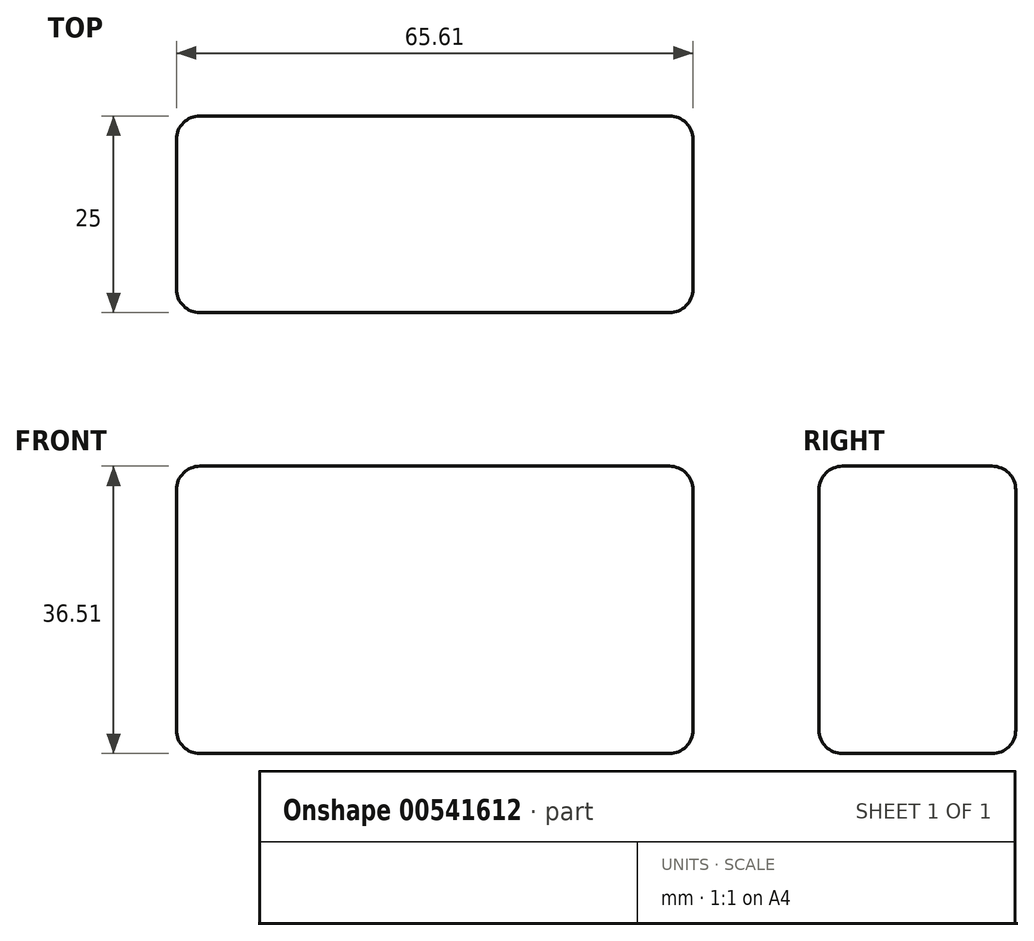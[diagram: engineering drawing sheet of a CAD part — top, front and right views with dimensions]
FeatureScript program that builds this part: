
annotation { "Feature Type Name" : "Feature", "Feature Type Description" : "" }
export const myFeature = defineFeature(function(context is Context, id is Id, definition is map)
    precondition{}
    {
        {
            var Q0;
            Q0=qCreatedBy(makeId("Front.planeOp"),FACE);
            var sketch = newSketch(context, id + "F0", { "sketchPlane" : qUnion([Q0])});
            skLineSegment(sketch, "E0.bottom", {"start": v(-30.55, 25.56) * mm, "end": v(35.06, 25.56) * mm});
            skLineSegment(sketch, "E0.top", {"start": v(-30.55, -10.95) * mm, "end": v(35.06, -10.95) * mm});
            skLineSegment(sketch, "E0.left", {"start": v(-30.55, 25.56) * mm, "end": v(-30.55, -10.95) * mm});
            skLineSegment(sketch, "E0.right", {"start": v(35.06, 25.56) * mm, "end": v(35.06, -10.95) * mm});
            skSolve(sketch);
        }
        {
            var Q0;
            Q0=makeQuery(id+"F0.imprint","IMPRINT",FACE,{"disambiguationData":[TD([[makeQuery(id+"F0.imprint","IMPRINT",EDGE,{"derivedFrom":sQuery(id+"F0.wireOp",EDGE,"E0.bottom")}),-1.0]])]});
            extrude(context, id + "F1", {"entities" : qUnion([Q0]), "depth" : 25 * mm, "offsetDistance" : 25 * mm});
        }
        {
            var Q0;
            Q0=makeQuery(id+"F1.opExtrude","CAP_EDGE",EDGE,{"disambiguationData":[OSD([sQuery(id+"F0.wireOp",EDGE,"E0.bottom")])],"isStart":false});
            var Q1;
            Q1=makeQuery(id+"F1.opExtrude","CAP_EDGE",EDGE,{"disambiguationData":[OSD([sQuery(id+"F0.wireOp",EDGE,"E0.bottom")])],"isStart":true});
            var Q2;
            Q2=makeQuery(id+"F1.opExtrude","CAP_EDGE",EDGE,{"disambiguationData":[OSD([sQuery(id+"F0.wireOp",EDGE,"E0.top")])],"isStart":false});
            var Q3;
            Q3=makeQuery(id+"F1.opExtrude","CAP_EDGE",EDGE,{"disambiguationData":[OSD([sQuery(id+"F0.wireOp",EDGE,"E0.right")])],"isStart":false});
            var Q4;
            Q4=makeQuery(id+"F1.opExtrude","SWEPT_EDGE",EDGE,{"disambiguationData":[OSD([sQuery(id+"F0.wireOp",EDGE,"E0.bottom"),sQuery(id+"F0.wireOp",EDGE,"E0.right")])]});
            var Q5;
            Q5=makeQuery(id+"F1.opExtrude","SWEPT_FACE",FACE,{"disambiguationData":[OSD([sQuery(id+"F0.wireOp",EDGE,"E0.top")])]});
            var Q6;
            Q6=makeQuery(id+"F1.opExtrude","CAP_EDGE",EDGE,{"disambiguationData":[OSD([sQuery(id+"F0.wireOp",EDGE,"E0.right")])],"isStart":true});
            var Q7;
            Q7=makeQuery(id+"F1.opExtrude","SWEPT_EDGE",EDGE,{"disambiguationData":[OSD([sQuery(id+"F0.wireOp",EDGE,"E0.bottom"),sQuery(id+"F0.wireOp",EDGE,"E0.left")])]});
            var Q8;
            Q8=makeQuery(id+"F1.opExtrude","CAP_EDGE",EDGE,{"disambiguationData":[OSD([sQuery(id+"F0.wireOp",EDGE,"E0.left")])],"isStart":false});
            var Q9;
            Q9=makeQuery(id+"F1.opExtrude","CAP_EDGE",EDGE,{"disambiguationData":[OSD([sQuery(id+"F0.wireOp",EDGE,"E0.left")])],"isStart":true});
            fillet(context, id + "F2", {"entities" : qUnion([Q0, Q1, Q2, Q3, Q4, Q5, Q6, Q7, Q8, Q9]), "radius" : 3 * mm, "tangentPropagation" : true, "allowEdgeOverflow" : false});
        }
    });
